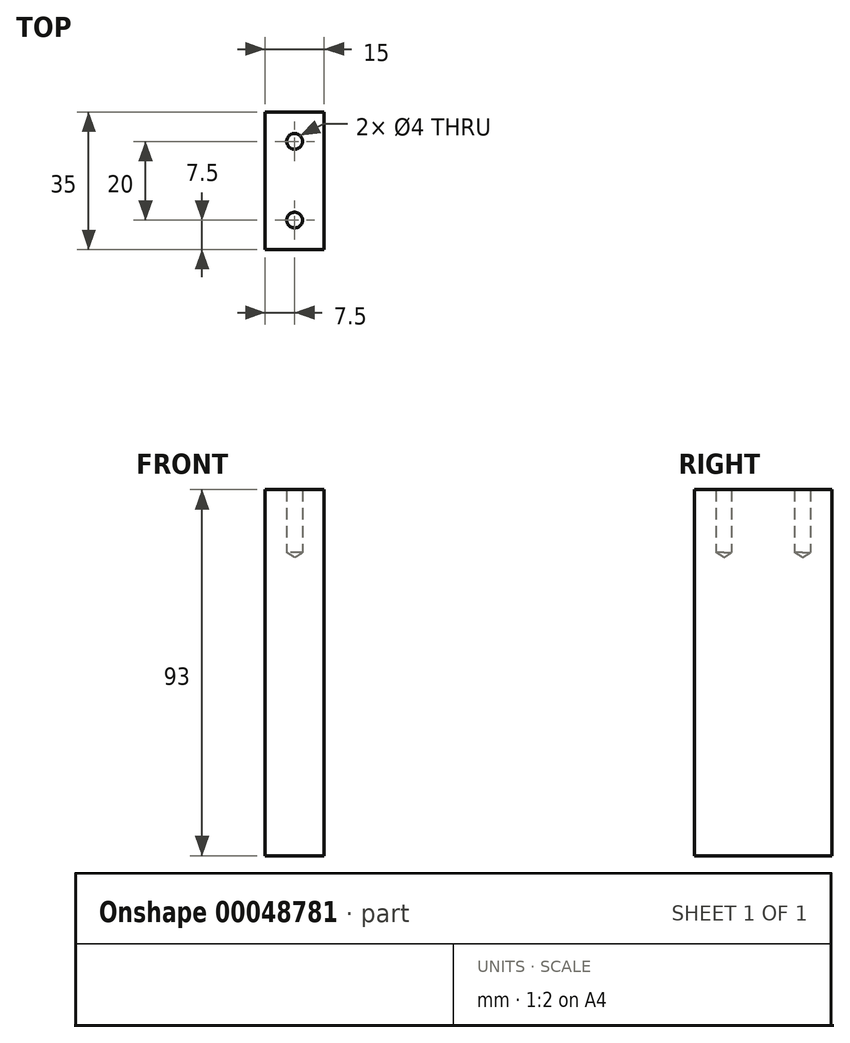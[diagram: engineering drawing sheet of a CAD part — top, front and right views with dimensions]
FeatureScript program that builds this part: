
annotation { "Feature Type Name" : "Feature", "Feature Type Description" : "" }
export const myFeature = defineFeature(function(context is Context, id is Id, definition is map)
    precondition{}
    {
        {
            var Q0;
            Q0=qCreatedBy(makeId("Right.planeOp"),FACE);
            var sketch = newSketch(context, id + "F0", { "sketchPlane" : qUnion([Q0])});
            skLineSegment(sketch, "E0.bottom", {"start": v(17.5, -46.5) * mm, "end": v(-17.5, -46.5) * mm});
            skLineSegment(sketch, "E0.top", {"start": v(17.5, 46.5) * mm, "end": v(-17.5, 46.5) * mm});
            skLineSegment(sketch, "E0.left", {"start": v(17.5, -46.5) * mm, "end": v(17.5, 46.5) * mm});
            skLineSegment(sketch, "E0.right", {"start": v(-17.5, -46.5) * mm, "end": v(-17.5, 46.5) * mm});
            skPoint(sketch, "E0.middle", {"position": v(0, 0) * mm});
            skSolve(sketch);
        }
        {
            var Q0;
            Q0=makeQuery(id+"F0.imprint","IMPRINT",FACE,{"disambiguationData":[TD([[makeQuery(id+"F0.imprint","IMPRINT",EDGE,{"derivedFrom":sQuery(id+"F0.wireOp",EDGE,"E0.bottom")}),-1.0]])]});
            extrude(context, id + "F1", {"entities" : qUnion([Q0]), "depth" : 15 * mm, "symmetric" : true});
        }
        {
            var Q0;
            Q0=makeQuery(id+"F1.opExtrude","SWEPT_FACE",FACE,{"disambiguationData":[OSD([sQuery(id+"F0.wireOp",EDGE,"E0.top")])]});
            var sketch = newSketch(context, id + "F2", { "sketchPlane" : qUnion([Q0])});
            skPoint(sketch, "E1", {"position": v(0, 10) * mm});
            skPoint(sketch, "E1.positionSnap0", {"position": v(0, 17.5) * mm});
            skPoint(sketch, "E2", {"position": v(0, -10) * mm});
            skPoint(sketch, "E2.positionSnap0", {"position": v(0, -17.5) * mm});
            skSolve(sketch);
        }
        {
            var Q0;
            Q0=sQuery(id+"F2.wireOp",VERTEX,"E1");
            var Q1;
            Q1=sQuery(id+"F2.wireOp",VERTEX,"E2");
            var Q2;
            Q2=makeQuery(id+"F1.opExtrude","SWEPT_BODY",BODY,{"disambiguationData":[OSD([sQuery(id+"F0.wireOp",EDGE,"E0.bottom"),sQuery(id+"F0.wireOp",EDGE,"E0.top"),sQuery(id+"F0.wireOp",EDGE,"E0.left"),sQuery(id+"F0.wireOp",EDGE,"E0.right")])]});
            hole(context, id + "F3", {"style" : HoleStyle.SIMPLE, "endStyle" : HoleEndStyle.BLIND, "standardTappedOrClearance" : lookupTablePath({ "standard" : "ISO", "engagement" : "75%", "pitch" : "1 mm", "size" : "M5", "type" : "Tapped" }), "standardBlindInLast" : lookupTablePath({ "standard" : "ISO", "engagement" : "75%", "pitch" : "1 mm", "size" : "M5", "type" : "Tapped" }), "holeDiameter" : 4 * mm, "holeDepth" : 16 * mm, "locations" : qUnion([Q0, Q1]), "scope" : qUnion([Q2]), "startStyle" : HoleStartStyle.PART});
        }
    });
